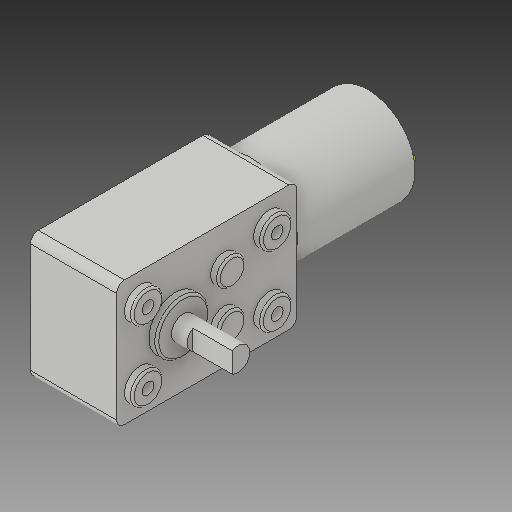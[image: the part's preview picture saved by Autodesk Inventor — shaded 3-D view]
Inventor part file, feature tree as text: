
AUTODESK INVENTOR PART (.ipt)
format: ipt  version: 2019 (Build 230136000, 136)  size: 362,496 bytes
history: native  units: mm
features: extrude x10, sketch x10, fillet x7, projected_geometry x6, other x1
ambient origin geometry x8: Origin, YZ Plane, XZ Plane, XY Plane, X Axis, Y Axis, Z Axis, Center Point
bodies: Body1 (feature_tree)
feature tree (34):
  other  "Твердое тело1"
  extrude  "Выдавливание1"  Depth=32.0mm
  fillet  "Сопряжение1"  Radius=46.0mm
  extrude  "Выдавливание2"  Depth=22.0mm TaperAngle=0.0deg
  extrude  "Выдавливание3"  Depth=2.0mm
  fillet  "Сопряжение2"  Radius=10.0mm
  extrude  "Выдавливание4"  Depth=14.0mm
  fillet  "Сопряжение3"  Radius=13.0mm
  extrude  "Выдавливание5"  Depth=0.2mm TaperAngle=0.0deg
  fillet  "Сопряжение4"  Radius=24.0mm
  extrude  "Выдавливание6"  Depth=31.0mm TaperAngle=0.0deg
  fillet  "Сопряжение5"  Radius=1.0mm
  extrude  "Выдавливание7"  Depth=0.5mm
  extrude  "Выдавливание8"  Depth=6.0mm
  extrude  "Выдавливание9"  Depth=1.0mm TaperAngle=0.0deg
  extrude  "Выдавливание10"  Depth=0.3mm
  fillet  "Сопряжение6"  Radius=0.2mm
  fillet  "Сопряжение7"  Radius=2.0mm
  sketch  "Эскиз1"
  sketch  "Эскиз2"
  sketch  "Эскиз3"
  sketch  "Эскиз4"
  sketch  "Эскиз5"
  projected_geometry  "Спроецированная петля1"
  projected_geometry  "Спроецированная петля2"
  sketch  "Эскиз6"
  sketch  "Эскиз7"
  projected_geometry  "Спроецированная петля3"
  projected_geometry  "Спроецированная петля4"
  sketch  "Эскиз8"
  projected_geometry  "Спроецированная петля5"
  sketch  "Эскиз9"
  projected_geometry  "Спроецированная петля6"
  sketch  "Эскиз10"
